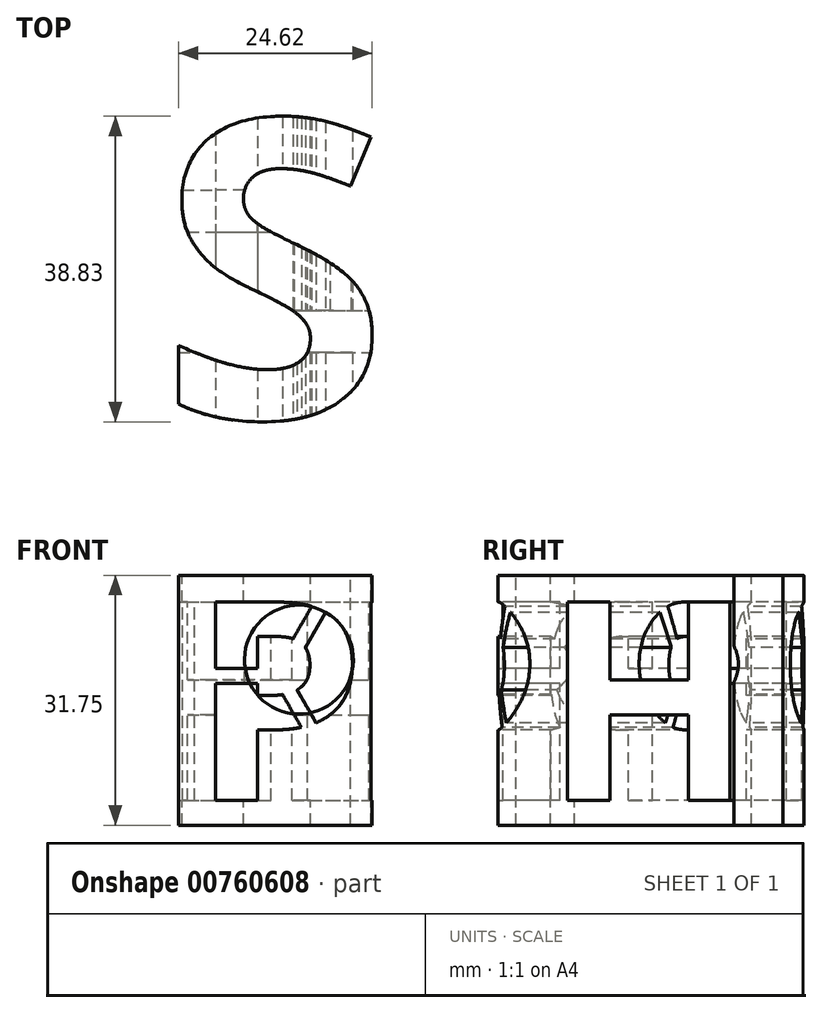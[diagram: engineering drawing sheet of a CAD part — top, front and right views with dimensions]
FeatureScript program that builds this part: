
annotation { "Feature Type Name" : "Feature", "Feature Type Description" : "" }
export const myFeature = defineFeature(function(context is Context, id is Id, definition is map)
    precondition{}
    {
        {
            var Q0;
            Q0=qCreatedBy(makeId("Front.planeOp"),FACE);
            var sketch = newSketch(context, id + "F0", { "sketchPlane" : qUnion([Q0])});
            skLineSegment(sketch, "E0.bottom", {"start": v(0, 0) * mm, "end": v(50.8, 0) * mm});
            skLineSegment(sketch, "E0.top", {"start": v(0, 31.75) * mm, "end": v(50.8, 31.75) * mm});
            skLineSegment(sketch, "E0.left", {"start": v(0, 0) * mm, "end": v(0, 31.75) * mm});
            skLineSegment(sketch, "E0.right", {"start": v(50.8, 0) * mm, "end": v(50.8, 31.75) * mm});
            skSolve(sketch);
        }
        {
            var Q0;
            Q0=makeQuery(id+"F0.imprint","IMPRINT",FACE,{"disambiguationData":[TD([[makeQuery(id+"F0.imprint","IMPRINT",EDGE,{"derivedFrom":sQuery(id+"F0.wireOp",EDGE,"E0.bottom")}),1.0]])]});
            extrude(context, id + "F1", {"entities" : qUnion([Q0]), "oppositeDirection" : true, "depth" : 50.8 * mm, "offsetDistance" : 25.4 * mm});
        }
        {
            var Q0;
            Q0=makeQuery(id+"F1.opExtrude","CAP_FACE",FACE,{"disambiguationData":[OSD([sQuery(id+"F0.wireOp",EDGE,"E0.bottom"),sQuery(id+"F0.wireOp",EDGE,"E0.top"),sQuery(id+"F0.wireOp",EDGE,"E0.left"),sQuery(id+"F0.wireOp",EDGE,"E0.right")])],"isStart":true});
            var sketch = newSketch(context, id + "F2", { "sketchPlane" : qUnion([Q0])});
            skText(sketch, "E1", { "text": "P", "fontName": "OpenSans-Bold.ttf"});
            skPoint(sketch, "E2", {"position": v(20.32, 18.99) * mm});
            skLineSegment(sketch, "E3.bottom", {"start": v(8.98, 19.94) * mm, "end": v(18.84, 19.94) * mm});
            skLineSegment(sketch, "E3.top", {"start": v(8.98, 18.04) * mm, "end": v(18.84, 18.04) * mm});
            skLineSegment(sketch, "E3.left", {"start": v(8.98, 19.94) * mm, "end": v(8.98, 18.04) * mm});
            skLineSegment(sketch, "E3.right", {"start": v(18.84, 19.94) * mm, "end": v(18.84, 18.04) * mm});
            skLineSegment(sketch, "E4.1.0", {"start": v(25.16, 8.7) * mm, "end": v(20.24, 17.23) * mm});
            skLineSegment(sketch, "E4.1.1", {"start": v(25.16, 8.7) * mm, "end": v(26.81, 9.65) * mm});
            skLineSegment(sketch, "E4.1.2", {"start": v(26.81, 9.65) * mm, "end": v(21.89, 18.18) * mm});
            skLineSegment(sketch, "E4.1.3", {"start": v(20.24, 17.23) * mm, "end": v(21.89, 18.18) * mm});
            skLineSegment(sketch, "E4.2.0", {"start": v(26.81, 28.33) * mm, "end": v(21.89, 19.8) * mm});
            skLineSegment(sketch, "E4.2.1", {"start": v(26.81, 28.33) * mm, "end": v(25.16, 29.28) * mm});
            skLineSegment(sketch, "E4.2.2", {"start": v(25.16, 29.28) * mm, "end": v(20.24, 20.75) * mm});
            skLineSegment(sketch, "E4.2.3", {"start": v(21.89, 19.8) * mm, "end": v(20.24, 20.75) * mm});
            skPoint(sketch, "E5", {"position": v(18.84, 18.99) * mm});
            skLineSegment(sketch, "E6", {"start": v(20.32, 18.99) * mm, "end": v(18.84, 18.99) * mm});
            const initialGuessF2  = {"E1": [0.0089, 0.00317, 1, 0, 0.0254]};
            skSetInitialGuess(sketch, initialGuessF2);
            skSolve(sketch);
        }
        {
            var Q0;
            {var subQ5=sQuery(id+"F2.wireOp",EDGE,"E1.sketch_text.stroke-5");Q0=makeQuery(id+"F2.imprint","IMPRINT",FACE,{"disambiguationData":[TD([[makeQuery(id+"F2.imprint","IMPRINT",EDGE,{"derivedFrom":subQ5}),-1.0]])]});}
            var Q1;
            {var subQ1=sQuery(id+"F2.wireOp",EDGE,"E1.sketch_text.stroke-2");Q1=makeQuery(id+"F2.imprint","IMPRINT",FACE,{"disambiguationData":[TD([[makeQuery(id+"F2.imprint","IMPRINT",EDGE,{"derivedFrom":subQ1}),-1.0]])]});}
            var Q2;
            {var subQ1=sQuery(id+"F2.wireOp",EDGE,"E1.sketch_text.stroke-0");Q2=makeQuery(id+"F2.imprint","IMPRINT",FACE,{"disambiguationData":[TD([[makeQuery(id+"F2.imprint","IMPRINT",EDGE,{"derivedFrom":subQ1}),-1.0]])]});}
            extrude(context, id + "F3", {"entities" : qUnion([Q0, Q1, Q2]), "operationType" : NewBodyOperationType.REMOVE, "endBound" : BoundingType.THROUGH_ALL, "oppositeDirection" : true, "depth" : 25.4 * mm, "offsetDistance" : 25.4 * mm});
        }
        {
            var Q0;
            Q0=makeQuery(id+"F1.opExtrude","SWEPT_FACE",FACE,{"disambiguationData":[OSD([sQuery(id+"F0.wireOp",EDGE,"E0.right")])]});
            var sketch = newSketch(context, id + "F4", { "sketchPlane" : qUnion([Q0])});
            skText(sketch, "E7", { "text": "H", "fontName": "OpenSans-Bold.ttf"});
            const initialGuessF4  = {"E7": [0.006, 0.00318, 1, 0, 0.0254]};
            skSetInitialGuess(sketch, initialGuessF4);
            skSolve(sketch);
        }
        {
            var Q0;
            Q0 = qSketchRegion(id + "F4", true);
            extrude(context, id + "F5", {"entities" : qUnion([Q0]), "operationType" : NewBodyOperationType.REMOVE, "endBound" : BoundingType.THROUGH_ALL, "oppositeDirection" : true, "depth" : 25.4 * mm, "offsetDistance" : 25.4 * mm});
        }
        {
            var Q0;
            Q0=makeQuery(id+"F1.opExtrude","SWEPT_FACE",FACE,{"disambiguationData":[OSD([sQuery(id+"F0.wireOp",EDGE,"E0.top")])]});
            var sketch = newSketch(context, id + "F6", { "sketchPlane" : qUnion([Q0])});
            skText(sketch, "E8", { "text": "S", "fontName": "OpenSans-Bold.ttf"});
            skPoint(sketch, "E9", {"position": v(7.43, 10.14) * mm});
            skPoint(sketch, "E10", {"position": v(32.17, 12.12) * mm});
            const initialGuessF6  = {"E8": [0.00494, 0.00086, 1, 0, 0.0381]};
            skSetInitialGuess(sketch, initialGuessF6);
            skSolve(sketch);
        }
        {
            var Q0;
            Q0=makeQuery(id+"F6.imprint","IMPRINT",FACE,{"disambiguationData":[TD([[makeQuery(id+"F6.imprint","IMPRINT",EDGE,{"derivedFrom":sQuery(id+"F6.wireOp",EDGE,"E8.sketch_text.stroke-0")}),1.0]])]});
            extrude(context, id + "F7", {"entities" : qUnion([Q0]), "operationType" : NewBodyOperationType.REMOVE, "endBound" : BoundingType.THROUGH_ALL, "oppositeDirection" : true, "depth" : 25.4 * mm, "offsetDistance" : 25.4 * mm});
        }
    });
